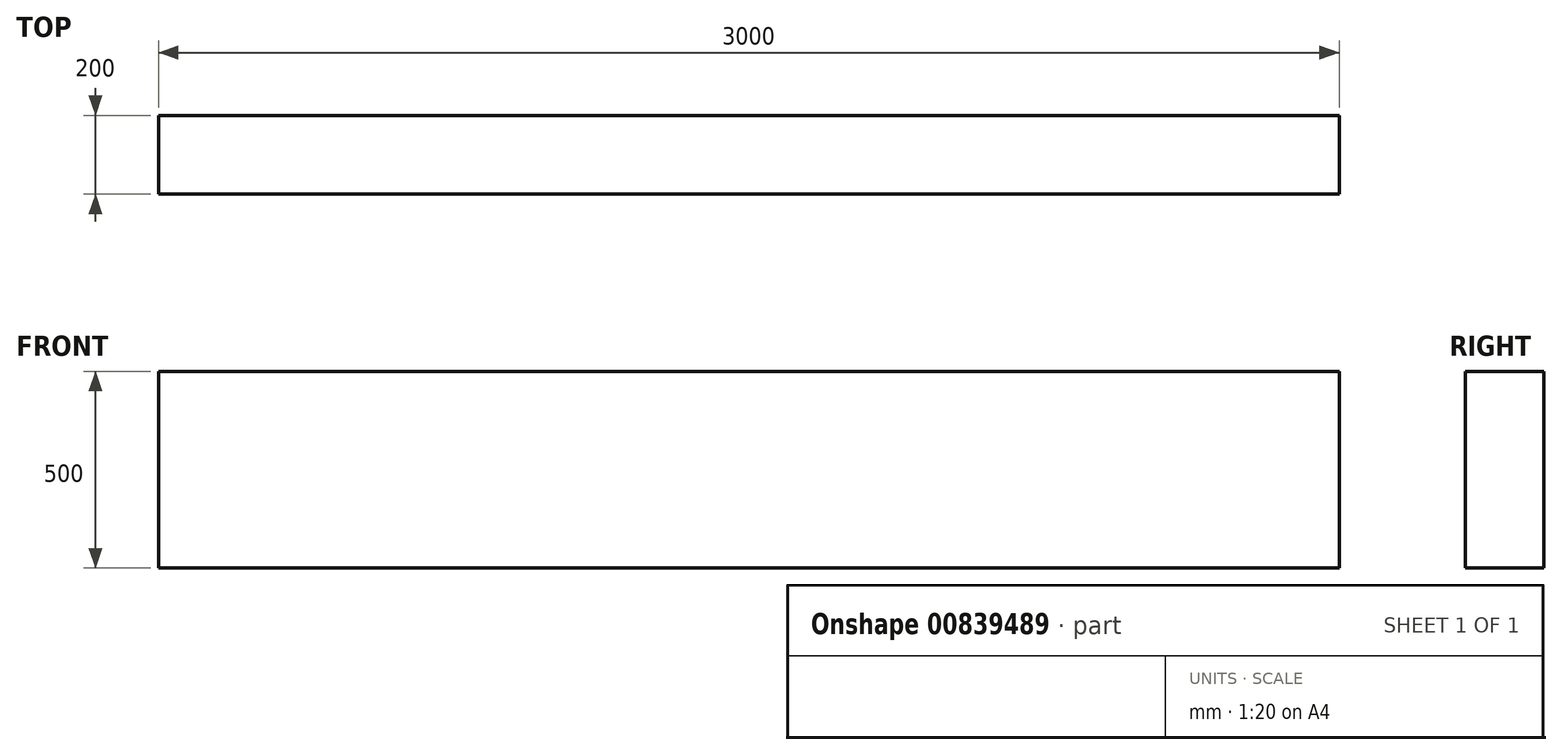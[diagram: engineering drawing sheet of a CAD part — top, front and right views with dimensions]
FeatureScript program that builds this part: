
annotation { "Feature Type Name" : "Feature", "Feature Type Description" : "" }
export const myFeature = defineFeature(function(context is Context, id is Id, definition is map)
    precondition{}
    {
        {
            var Q0;
            Q0=qCreatedBy(makeId("Front.planeOp"),FACE);
            var sketch = newSketch(context, id + "F0", { "sketchPlane" : qUnion([Q0])});
            skLineSegment(sketch, "E0.bottom", {"start": v(1500, -250) * mm, "end": v(-1500, -250) * mm});
            skLineSegment(sketch, "E0.top", {"start": v(1500, 250) * mm, "end": v(-1500, 250) * mm});
            skLineSegment(sketch, "E0.left", {"start": v(1500, -250) * mm, "end": v(1500, 250) * mm});
            skLineSegment(sketch, "E0.right", {"start": v(-1500, -250) * mm, "end": v(-1500, 250) * mm});
            skPoint(sketch, "E0.middle", {"position": v(0, 0) * mm});
            skSolve(sketch);
        }
        {
            var Q0;
            Q0=makeQuery(id+"F0.imprint","IMPRINT",FACE,{"disambiguationData":[TD([[makeQuery(id+"F0.imprint","IMPRINT",EDGE,{"derivedFrom":sQuery(id+"F0.wireOp",EDGE,"E0.bottom")}),-1.0]])]});
            extrude(context, id + "F1", {"entities" : qUnion([Q0]), "depth" : 200 * mm, "offsetDistance" : 25 * mm});
        }
    });
